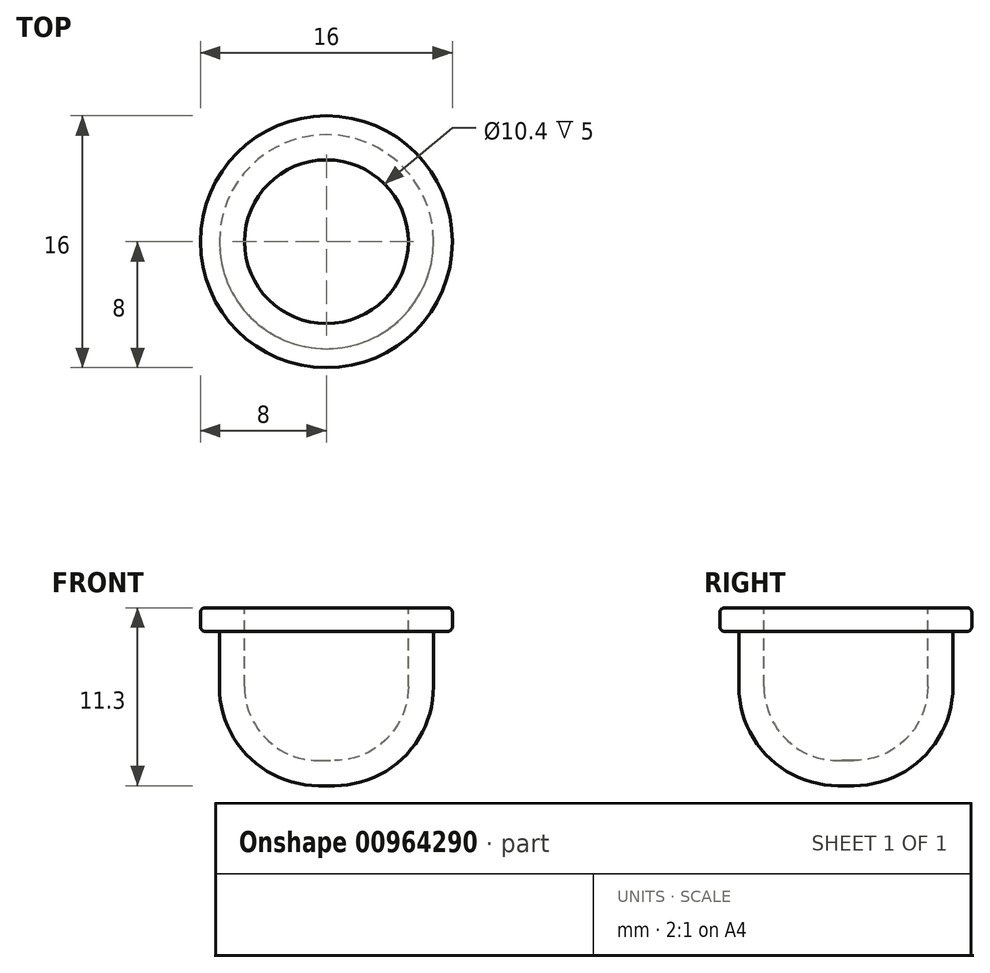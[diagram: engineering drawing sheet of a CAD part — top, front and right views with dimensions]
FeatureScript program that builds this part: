
annotation { "Feature Type Name" : "Feature", "Feature Type Description" : "" }
export const myFeature = defineFeature(function(context is Context, id is Id, definition is map)
    precondition{}
    {
        {
            var Q0;
            Q0=qCreatedBy(makeId("Front.planeOp"),FACE);
            var sketch = newSketch(context, id + "F0", { "sketchPlane" : qUnion([Q0])});
            skLineSegment(sketch, "E0", {"start": v(0, 0) * mm, "end": v(0, -11.3) * mm});
            skLineSegment(sketch, "E1", {"start": v(0, 0) * mm, "end": v(8, 0) * mm});
            skLineSegment(sketch, "E2", {"start": v(8, 0) * mm, "end": v(8, -1.5) * mm});
            skLineSegment(sketch, "E3", {"start": v(8, -1.5) * mm, "end": v(6.8, -1.5) * mm});
            skLineSegment(sketch, "E4", {"start": v(6.8, -1.5) * mm, "end": v(6.8, -11.3) * mm});
            skLineSegment(sketch, "E5", {"start": v(6.8, -11.3) * mm, "end": v(0, -11.3) * mm});
            skSolve(sketch);
        }
        {
            var Q0;
            Q0 = qSketchRegion(id + "F0", true);
            var Q1;
            Q1=sQuery(id+"F0.wireOp",EDGE,"E0");
            revolve(context, id + "F1", {"surfaceOperationType" : NewSurfaceOperationType.NEW, "entities" : qUnion([Q0]), "axis" : qUnion([Q1]), "revolveType" : RevolveType.FULL});
        }
        {
            var Q0;
            Q0=makeQuery(id+"F1.opRevolve","SWEPT_EDGE",EDGE,{"disambiguationData":[OSD([sQuery(id+"F0.wireOp",EDGE,"E4"),sQuery(id+"F0.wireOp",EDGE,"E5")])]});
            fillet(context, id + "F2", {"entities" : qUnion([Q0]), "radius" : 6.3 * mm, "tangentPropagation" : true, "allowEdgeOverflow" : false});
        }
        {
            var Q0;
            Q0=makeQuery(id+"F1.opRevolve","SWEPT_FACE",FACE,{"disambiguationData":[OSD([sQuery(id+"F0.wireOp",EDGE,"E2")])]});
            fillet(context, id + "F3", {"entities" : qUnion([Q0]), "radius" : .3 * mm, "tangentPropagation" : true, "allowEdgeOverflow" : false});
        }
        {
            var Q0;
            Q0=makeQuery(id+"F1.opRevolve","SWEPT_FACE",FACE,{"disambiguationData":[OSD([sQuery(id+"F0.wireOp",EDGE,"E1")])]});
            shell(context, id + "F4", {"entities" : qUnion([Q0]), "thickness" : 1.6 * mm});
        }
    });
